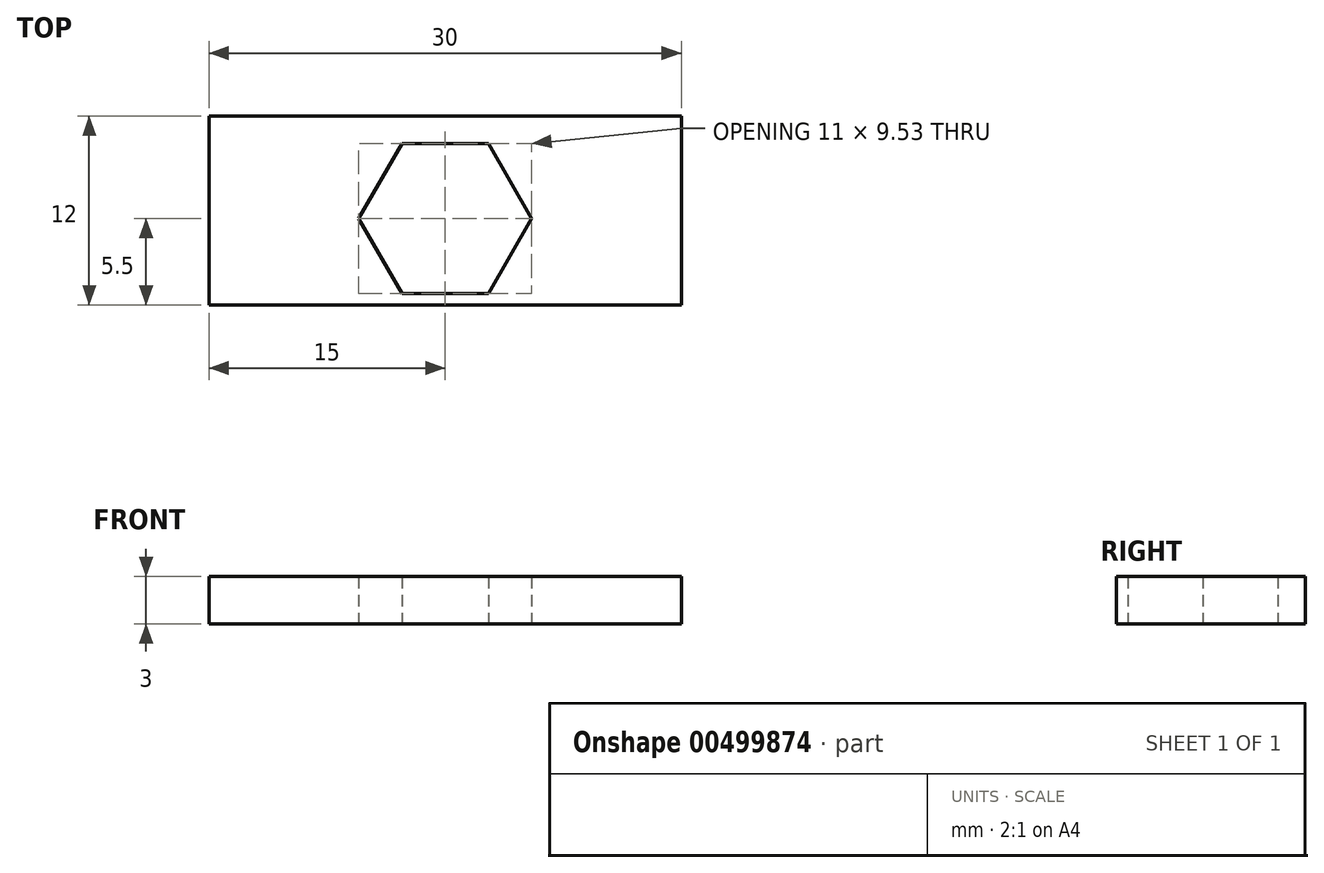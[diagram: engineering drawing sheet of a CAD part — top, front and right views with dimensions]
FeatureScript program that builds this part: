
annotation { "Feature Type Name" : "Feature", "Feature Type Description" : "" }
export const myFeature = defineFeature(function(context is Context, id is Id, definition is map)
    precondition{}
    {
        {
            var Q0;
            Q0=qCreatedBy(makeId("Top.planeOp"),FACE);
            var sketch = newSketch(context, id + "F0", { "sketchPlane" : qUnion([Q0])});
            skLineSegment(sketch, "E0.bottom", {"start": v(15, -6) * mm, "end": v(-15, -6) * mm});
            skLineSegment(sketch, "E0.top", {"start": v(15, 6) * mm, "end": v(-15, 6) * mm});
            skLineSegment(sketch, "E0.left", {"start": v(15, -6) * mm, "end": v(15, 6) * mm});
            skLineSegment(sketch, "E0.right", {"start": v(-15, -6) * mm, "end": v(-15, 6) * mm});
            skPoint(sketch, "E0.middle", {"position": v(0, 0) * mm});
            skCircle(sketch, "E1.cCircle", {"center": v(0, -0.5) * mm, "radius": 4.76 * mm, "construction": true});
            skLineSegment(sketch, "E1.0", {"start": v(2.75, -5.26) * mm, "end": v(-2.75, -5.26) * mm});
            skLineSegment(sketch, "E1.1", {"start": v(-2.75, -5.26) * mm, "end": v(-5.5, -0.5) * mm});
            skLineSegment(sketch, "E1.2", {"start": v(-5.5, -0.5) * mm, "end": v(-2.75, 4.26) * mm});
            skLineSegment(sketch, "E1.3", {"start": v(-2.75, 4.26) * mm, "end": v(2.75, 4.26) * mm});
            skLineSegment(sketch, "E1.4", {"start": v(2.75, 4.26) * mm, "end": v(5.5, -0.5) * mm});
            skLineSegment(sketch, "E1.5", {"start": v(5.5, -0.5) * mm, "end": v(2.75, -5.26) * mm});
            skPoint(sketch, "E1.0.midPoint", {"position": v(0, -5.26) * mm});
            skPoint(sketch, "E2", {"position": v(0, 6) * mm});
            skSolve(sketch);
        }
        {
            var Q0;
            Q0=qSketchRegion(id+"F0",true);
            extrude(context, id + "F1", {"entities" : qUnion([Q0]), "depth" : 3 * mm, "offsetDistance" : 25 * mm});
        }
    });
